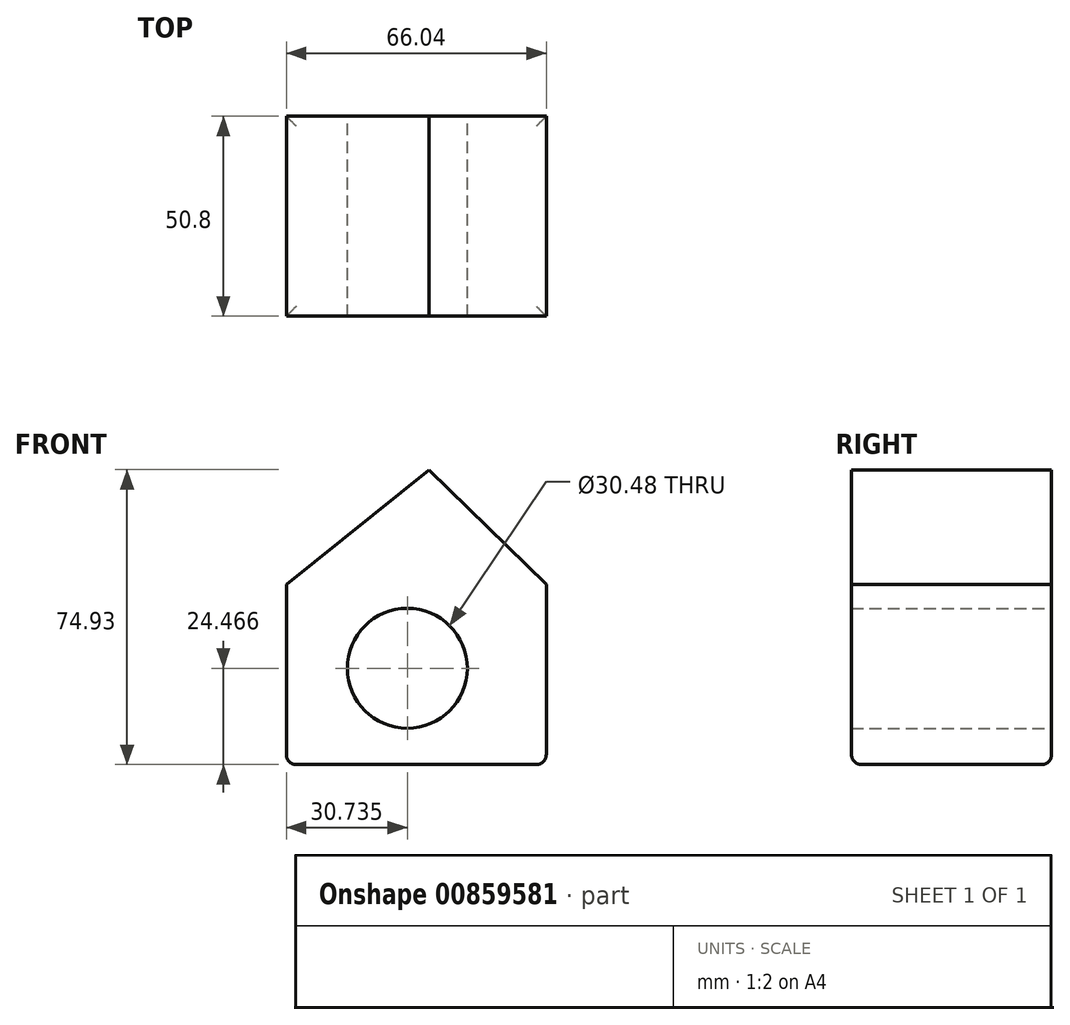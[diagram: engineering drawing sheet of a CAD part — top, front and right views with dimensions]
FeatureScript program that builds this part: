
annotation { "Feature Type Name" : "Feature", "Feature Type Description" : "" }
export const myFeature = defineFeature(function(context is Context, id is Id, definition is map)
    precondition{}
    {
        {
            var Q0;
            Q0=qCreatedBy(makeId("Front.planeOp"),FACE);
            var sketch = newSketch(context, id + "F0", { "sketchPlane" : qUnion([Q0])});
            skLineSegment(sketch, "E0.bottom", {"start": v(0, 0) * mm, "end": v(66.04, 0) * mm});
            skLineSegment(sketch, "E0.top", {"start": v(0, -45.72) * mm, "end": v(66.04, -45.72) * mm});
            skLineSegment(sketch, "E0.left", {"start": v(0, 0) * mm, "end": v(0, -45.72) * mm});
            skLineSegment(sketch, "E0.right", {"start": v(66.04, 0) * mm, "end": v(66.04, -45.72) * mm});
            skLineSegment(sketch, "E1", {"start": v(0, 0) * mm, "end": v(36.24, 29.2) * mm});
            skLineSegment(sketch, "E2", {"start": v(36.24, 29.2) * mm, "end": v(66.04, 0) * mm});
            skCircle(sketch, "E3", {"center": v(30.73, -21.25) * mm, "radius": 15.24 * mm});
            skSolve(sketch);
        }
        {
            var Q0;
            Q0 = qSketchRegion(id + "F0", true);
            extrude(context, id + "F1", {"entities" : qUnion([Q0]), "depth" : 50.8 * mm, "offsetDistance" : 25.4 * mm});
        }
        {
            var Q0;
            Q0=makeQuery(id+"F1.opExtrude","CAP_EDGE",EDGE,{"disambiguationData":[OSD([sQuery(id+"F0.wireOp",EDGE,"E0.top")])],"isStart":false});
            var Q1;
            Q1=makeQuery(id+"F1.opExtrude","SWEPT_EDGE",EDGE,{"disambiguationData":[OSD([sQuery(id+"F0.wireOp",EDGE,"E0.top"),sQuery(id+"F0.wireOp",EDGE,"E0.right")])]});
            var Q2;
            Q2=makeQuery(id+"F1.opExtrude","CAP_EDGE",EDGE,{"disambiguationData":[OSD([sQuery(id+"F0.wireOp",EDGE,"E0.top")])],"isStart":true});
            var Q3;
            Q3=makeQuery(id+"F1.opExtrude","SWEPT_EDGE",EDGE,{"disambiguationData":[OSD([sQuery(id+"F0.wireOp",EDGE,"E0.top"),sQuery(id+"F0.wireOp",EDGE,"E0.left")])]});
            fillet(context, id + "F2", {"entities" : qUnion([Q0, Q1, Q2, Q3]), "radius" : 2.54 * mm, "tangentPropagation" : true, "allowEdgeOverflow" : false});
        }
    });
